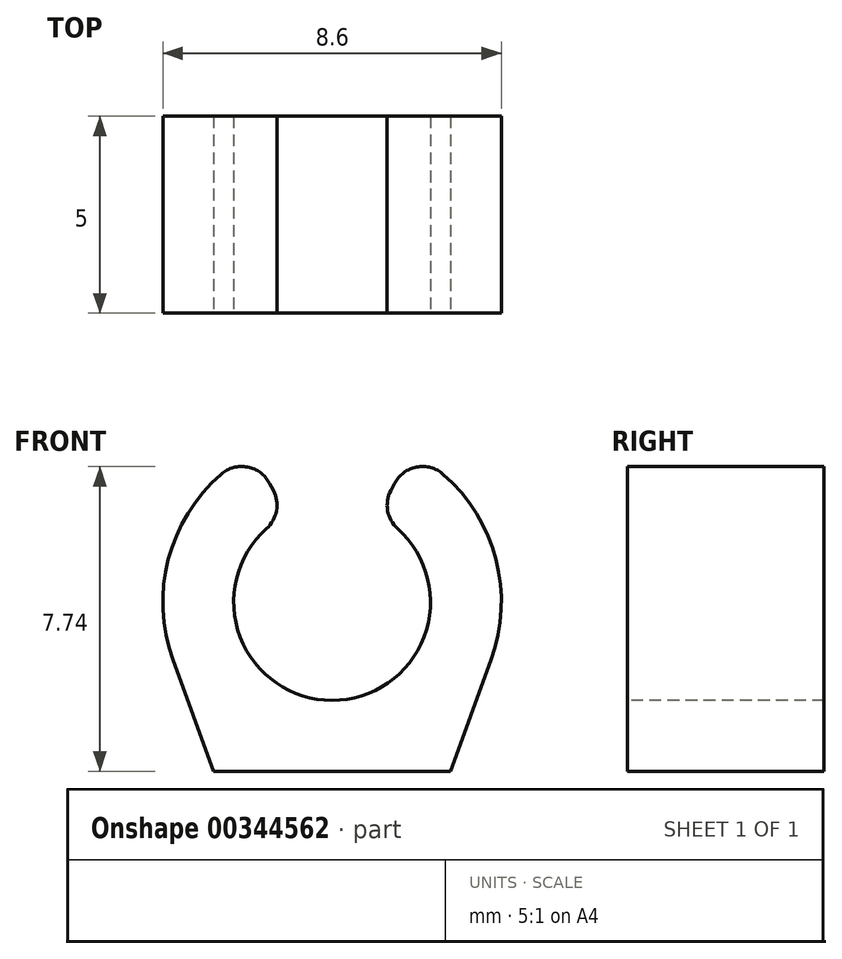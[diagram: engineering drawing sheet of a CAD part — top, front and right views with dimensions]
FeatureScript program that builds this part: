
annotation { "Feature Type Name" : "Feature", "Feature Type Description" : "" }
export const myFeature = defineFeature(function(context is Context, id is Id, definition is map)
    precondition{}
    {
        {
            var Q0;
            Q0=qCreatedBy(makeId("Front.planeOp"),FACE);
            var sketch = newSketch(context, id + "F0", { "sketchPlane" : qUnion([Q0])});
            skArc(sketch, "E0", {"start": v(-1.67, 1.86) * mm, "mid": v(0, -2.5) * mm, "end": v(1.67, 1.86) * mm});
            skArc(sketch, "E1.0", {"start": v(-2.82, 3.25) * mm, "mid": v(0, -4.3) * mm, "end": v(2.82, 3.25) * mm});
            skLineSegment(sketch, "E2", {"start": v(1.5, 2.83) * mm, "end": v(1.59, 3.01) * mm});
            skLineSegment(sketch, "E3.MirrorCS", {"start": v(-1.5, 2.83) * mm, "end": v(-1.59, 3.01) * mm});
            skPoint(sketch, "E4.visualSharp", {"position": v(-1.17, 2.21) * mm});
            skArc(sketch, "E4.filletArc", {"start": v(-1.67, 1.86) * mm, "mid": v(-1.41, 2.32) * mm, "end": v(-1.5, 2.83) * mm});
            skPoint(sketch, "E5.visualSharp", {"position": v(-2, 3.8) * mm});
            skArc(sketch, "E5.filletArc", {"start": v(-1.59, 3.01) * mm, "mid": v(-2.15, 3.43) * mm, "end": v(-2.82, 3.25) * mm});
            skPoint(sketch, "E6.visualSharp", {"position": v(1.17, 2.21) * mm});
            skArc(sketch, "E6.filletArc", {"start": v(1.5, 2.83) * mm, "mid": v(1.41, 2.32) * mm, "end": v(1.67, 1.86) * mm});
            skPoint(sketch, "E7.visualSharp", {"position": v(2, 3.8) * mm});
            skArc(sketch, "E7.filletArc", {"start": v(2.82, 3.25) * mm, "mid": v(2.15, 3.43) * mm, "end": v(1.59, 3.01) * mm});
            skLineSegment(sketch, "E8", {"start": v(-4.04, -1.47) * mm, "end": v(-3.01, -4.3) * mm});
            skLineSegment(sketch, "E9", {"start": v(-3.01, -4.3) * mm, "end": v(0, -4.3) * mm});
            skPoint(sketch, "E9.endSnap0", {"position": v(0, -2.5) * mm});
            skLineSegment(sketch, "E10.MirrorCS", {"start": v(3.01, -4.3) * mm, "end": v(0, -4.3) * mm});
            skLineSegment(sketch, "E11.MirrorCS", {"start": v(4.04, -1.47) * mm, "end": v(3.01, -4.3) * mm});
            skLineSegment(sketch, "E12", {"start": v(3.67, -2.5) * mm, "end": v(-3.67, -2.5) * mm});
            skSolve(sketch);
        }
        {
            var Q0;
            Q0=makeQuery(id+"F0.imprint","IMPRINT",FACE,{"disambiguationData":[TD([[makeQuery(id+"F0.imprint","IMPRINT",EDGE,{"derivedFrom":sQuery(id+"F0.wireOp",EDGE,"E0")}),-1.0]])]});
            var Q1;
            {var subQ0=sQuery(id+"F0.wireOp",EDGE,"E8");Q1=makeQuery(id+"F0.imprint","IMPRINT",FACE,{"disambiguationData":[TD([[makeQuery(id+"F0.imprint","IMPRINT",EDGE,{"derivedFrom":subQ0}),1.0]])]});}
            var Q2;
            {var subQ0=sQuery(id+"F0.wireOp",EDGE,"E10.MirrorCS");Q2=makeQuery(id+"F0.imprint","IMPRINT",FACE,{"disambiguationData":[TD([[makeQuery(id+"F0.imprint","IMPRINT",EDGE,{"derivedFrom":subQ0}),-1.0]])]});}
            var Q3;
            {var subQ2=sQuery(id+"F0.wireOp",EDGE,"E12");var subQ5=makeQuery(id+"F0.imprint","INTERSECT",VERTEX,{"derivedFrom":[sQuery(id+"F0.wireOp",EDGE,"E0"),subQ2]});Q3=makeQuery(id+"F0.imprint","IMPRINT",FACE,{"disambiguationData":[TD([[makeQuery(id+"F0.imprint","IMPRINT",EDGE,{"disambiguationData":[TD([[subQ5,1.0]])],"derivedFrom":subQ2}),1.0]])]});}
            var Q4;
            {var subQ0=sQuery(id+"F0.wireOp",EDGE,"E9");Q4=makeQuery(id+"F0.imprint","IMPRINT",FACE,{"disambiguationData":[TD([[makeQuery(id+"F0.imprint","IMPRINT",EDGE,{"derivedFrom":subQ0}),1.0]])]});}
            var Q5;
            {var subQ0=sQuery(id+"F0.wireOp",EDGE,"E11.MirrorCS");var subQ1=sQuery(id+"F0.wireOp",EDGE,"E1.0");var subQ2=makeQuery(id+"F0.imprint","INTERSECT",VERTEX,{"derivedFrom":[subQ1,subQ0]});Q5=makeQuery(id+"F0.imprint","IMPRINT",FACE,{"disambiguationData":[TD([[makeQuery(id+"F0.imprint","IMPRINT",EDGE,{"disambiguationData":[TD([[subQ2,1.0]])],"derivedFrom":subQ1}),-1.0]])]});}
            extrude(context, id + "F1", {"entities" : qUnion([Q0, Q1, Q2, Q3, Q4, Q5]), "oppositeDirection" : true, "depth" : 5 * mm, "symmetric" : true});
        }
    });
